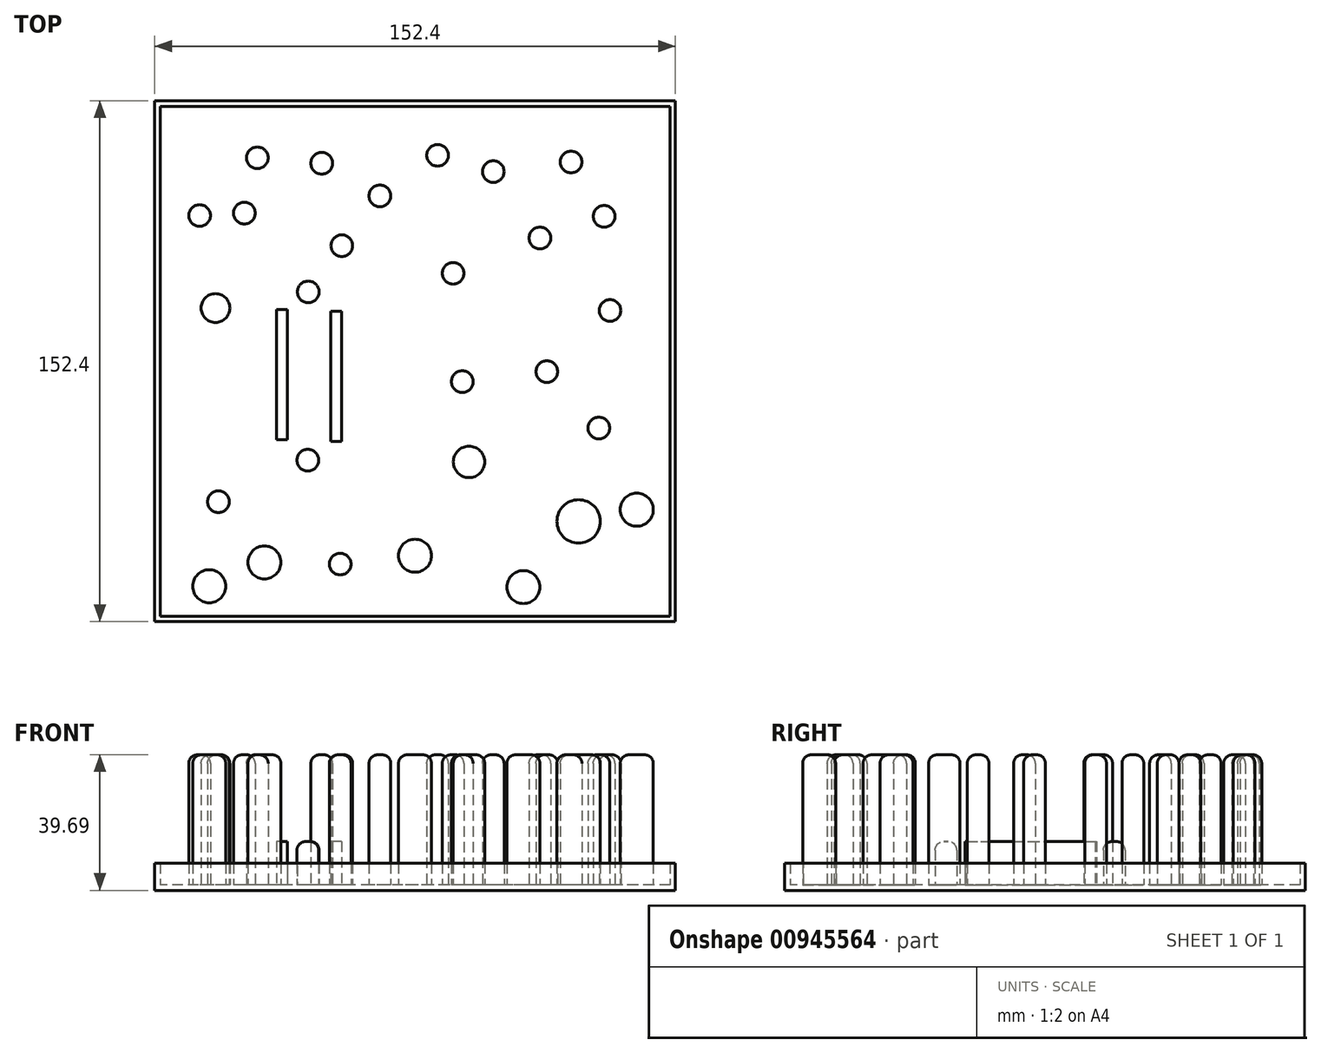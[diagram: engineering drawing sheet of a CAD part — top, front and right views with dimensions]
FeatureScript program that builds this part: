
annotation { "Feature Type Name" : "Feature", "Feature Type Description" : "" }
export const myFeature = defineFeature(function(context is Context, id is Id, definition is map)
    precondition{}
    {
        {
            var Q0;
            Q0=qCreatedBy(makeId("Top.planeOp"),FACE);
            var sketch = newSketch(context, id + "F0", { "sketchPlane" : qUnion([Q0])});
            skLineSegment(sketch, "E0.bottom", {"start": v(76.2, 76.2) * mm, "end": v(-76.2, 76.2) * mm});
            skLineSegment(sketch, "E0.top", {"start": v(76.2, -76.2) * mm, "end": v(-76.2, -76.2) * mm});
            skLineSegment(sketch, "E0.left", {"start": v(76.2, 76.2) * mm, "end": v(76.2, -76.2) * mm});
            skLineSegment(sketch, "E0.right", {"start": v(-76.2, 76.2) * mm, "end": v(-76.2, -76.2) * mm});
            skPoint(sketch, "E0.middle", {"position": v(0, 0) * mm});
            skSolve(sketch);
        }
        {
            var Q0;
            Q0=makeQuery(id+"F0.imprint","IMPRINT",FACE,{"disambiguationData":[TD([[makeQuery(id+"F0.imprint","IMPRINT",EDGE,{"derivedFrom":sQuery(id+"F0.wireOp",EDGE,"E0.bottom")}),1.0]])]});
            extrude(context, id + "F1", {"entities" : qUnion([Q0]), "depth" : 1.59 * mm, "offsetDistance" : 25.4 * mm});
        }
        {
            var Q0;
            Q0=makeQuery(id+"F1.opExtrude","CAP_FACE",FACE,{"disambiguationData":[OSD([sQuery(id+"F0.wireOp",EDGE,"E0.bottom"),sQuery(id+"F0.wireOp",EDGE,"E0.top"),sQuery(id+"F0.wireOp",EDGE,"E0.left"),sQuery(id+"F0.wireOp",EDGE,"E0.right")])],"isStart":false});
            var sketch = newSketch(context, id + "F2", { "sketchPlane" : qUnion([Q0])});
            skCircle(sketch, "E1", {"center": v(55.35, 42.37) * mm, "radius": 3.18 * mm});
            skLineSegment(sketch, "E2.bottom", {"start": v(74.61, 74.61) * mm, "end": v(-74.61, 74.61) * mm});
            skLineSegment(sketch, "E2.top", {"start": v(74.61, -74.61) * mm, "end": v(-74.61, -74.61) * mm});
            skLineSegment(sketch, "E2.left", {"start": v(74.61, 74.61) * mm, "end": v(74.61, -74.61) * mm});
            skLineSegment(sketch, "E2.right", {"start": v(-74.61, 74.61) * mm, "end": v(-74.61, -74.61) * mm});
            skPoint(sketch, "E2.middle", {"position": v(0, 0) * mm});
            skCircle(sketch, "E3", {"center": v(15.8, -29.49) * mm, "radius": 4.6 * mm});
            skCircle(sketch, "E4", {"center": v(53.8, -19.58) * mm, "radius": 3.18 * mm});
            skCircle(sketch, "E5", {"center": v(-31.25, 20.26) * mm, "radius": 3.18 * mm});
            skCircle(sketch, "E6", {"center": v(36.56, 36.04) * mm, "radius": 3.18 * mm});
            skCircle(sketch, "E7", {"center": v(-31.4, -28.99) * mm, "radius": 3.18 * mm});
            skLineSegment(sketch, "E8.bottom", {"start": v(-21.54, -23.45) * mm, "end": v(-24.72, -23.45) * mm});
            skLineSegment(sketch, "E8.top", {"start": v(-21.54, 14.65) * mm, "end": v(-24.72, 14.65) * mm});
            skLineSegment(sketch, "E8.left", {"start": v(-21.54, -23.45) * mm, "end": v(-21.54, 14.65) * mm});
            skLineSegment(sketch, "E8.right", {"start": v(-24.72, -23.45) * mm, "end": v(-24.72, 14.65) * mm});
            skLineSegment(sketch, "E9.bottom", {"start": v(-37.42, -22.96) * mm, "end": v(-40.6, -22.96) * mm});
            skLineSegment(sketch, "E9.top", {"start": v(-37.42, 15.14) * mm, "end": v(-40.6, 15.14) * mm});
            skLineSegment(sketch, "E9.left", {"start": v(-37.42, -22.96) * mm, "end": v(-37.42, 15.14) * mm});
            skLineSegment(sketch, "E9.right", {"start": v(-40.6, -22.96) * mm, "end": v(-40.6, 15.14) * mm});
            skCircle(sketch, "E10", {"center": v(11.14, 25.72) * mm, "radius": 3.18 * mm});
            skCircle(sketch, "E11", {"center": v(31.72, -66.13) * mm, "radius": 4.83 * mm});
            skCircle(sketch, "E12", {"center": v(-10.29, 48.37) * mm, "radius": 3.18 * mm});
            skCircle(sketch, "E13", {"center": v(22.9, 55.47) * mm, "radius": 3.18 * mm});
            skCircle(sketch, "E14", {"center": v(38.57, -3.06) * mm, "radius": 3.17 * mm});
            skCircle(sketch, "E15", {"center": v(-49.96, 43.35) * mm, "radius": 3.18 * mm});
            skCircle(sketch, "E16", {"center": v(-60.25, -65.88) * mm, "radius": 4.83 * mm});
            skCircle(sketch, "E17", {"center": v(-21.92, -59.4) * mm, "radius": 3.18 * mm});
            skCircle(sketch, "E18", {"center": v(-21.43, 33.8) * mm, "radius": 3.18 * mm});
            skCircle(sketch, "E19", {"center": v(0, -56.94) * mm, "radius": 4.83 * mm});
            skCircle(sketch, "E20", {"center": v(6.61, 60.25) * mm, "radius": 3.18 * mm});
            skCircle(sketch, "E21", {"center": v(-46.17, 59.51) * mm, "radius": 3.18 * mm});
            skCircle(sketch, "E22", {"center": v(-58.41, 15.55) * mm, "radius": 4.21 * mm});
            skCircle(sketch, "E23", {"center": v(-57.56, -41.15) * mm, "radius": 3.18 * mm});
            skCircle(sketch, "E24", {"center": v(-44.08, -58.9) * mm, "radius": 4.83 * mm});
            skCircle(sketch, "E25", {"center": v(-63.07, 42.62) * mm, "radius": 3.18 * mm});
            skCircle(sketch, "E26", {"center": v(-27.3, 57.92) * mm, "radius": 3.18 * mm});
            skCircle(sketch, "E27", {"center": v(47.88, -46.9) * mm, "radius": 6.35 * mm});
            skCircle(sketch, "E28", {"center": v(13.84, -6) * mm, "radius": 3.18 * mm});
            skCircle(sketch, "E29", {"center": v(57.07, 14.82) * mm, "radius": 3.18 * mm});
            skCircle(sketch, "E30", {"center": v(45.68, 58.29) * mm, "radius": 3.18 * mm});
            skCircle(sketch, "E31", {"center": v(64.9, -43.47) * mm, "radius": 4.83 * mm});
            skSolve(sketch);
        }
        {
            var Q0;
            Q0=makeQuery(id+"F2.imprint","IMPRINT",FACE,{"disambiguationData":[TD([[makeQuery(id+"F2.imprint","IMPRINT",EDGE,{"derivedFrom":sQuery(id+"F2.wireOp",EDGE,"E2.bottom")}),-1.0]])]});
            extrude(context, id + "F3", {"entities" : qUnion([Q0]), "operationType" : NewBodyOperationType.ADD, "depth" : 6.35 * mm, "offsetDistance" : 25.4 * mm});
        }
        {
            var Q0;
            Q0=makeQuery(id+"F2.imprint","IMPRINT",FACE,{"disambiguationData":[TD([[makeQuery(id+"F2.imprint","IMPRINT",EDGE,{"derivedFrom":sQuery(id+"F2.wireOp",EDGE,"E7")}),1.0]])]});
            var Q1;
            Q1=makeQuery(id+"F2.imprint","IMPRINT",FACE,{"disambiguationData":[TD([[makeQuery(id+"F2.imprint","IMPRINT",EDGE,{"derivedFrom":sQuery(id+"F2.wireOp",EDGE,"E5")}),1.0]])]});
            var Q2;
            Q2=makeQuery(id+"F2.imprint","IMPRINT",FACE,{"disambiguationData":[TD([[makeQuery(id+"F2.imprint","IMPRINT",EDGE,{"derivedFrom":sQuery(id+"F2.wireOp",EDGE,"E8.bottom")}),-1.0]])]});
            var Q3;
            Q3=makeQuery(id+"F2.imprint","IMPRINT",FACE,{"disambiguationData":[TD([[makeQuery(id+"F2.imprint","IMPRINT",EDGE,{"derivedFrom":sQuery(id+"F2.wireOp",EDGE,"E9.bottom")}),-1.0]])]});
            extrude(context, id + "F4", {"entities" : qUnion([Q0, Q1, Q2, Q3]), "operationType" : NewBodyOperationType.ADD, "depth" : 12.7 * mm, "offsetDistance" : 25.4 * mm});
        }
        {
            var Q0;
            Q0=makeQuery(id+"F2.imprint","IMPRINT",FACE,{"disambiguationData":[TD([[makeQuery(id+"F2.imprint","IMPRINT",EDGE,{"derivedFrom":sQuery(id+"F2.wireOp",EDGE,"E3")}),1.0]])]});
            var Q1;
            Q1=makeQuery(id+"F2.imprint","IMPRINT",FACE,{"disambiguationData":[TD([[makeQuery(id+"F2.imprint","IMPRINT",EDGE,{"derivedFrom":sQuery(id+"F2.wireOp",EDGE,"E4")}),1.0]])]});
            var Q2;
            Q2=makeQuery(id+"F2.imprint","IMPRINT",FACE,{"disambiguationData":[TD([[makeQuery(id+"F2.imprint","IMPRINT",EDGE,{"derivedFrom":sQuery(id+"F2.wireOp",EDGE,"E6")}),1.0]])]});
            var Q3;
            Q3=makeQuery(id+"F2.imprint","IMPRINT",FACE,{"disambiguationData":[TD([[makeQuery(id+"F2.imprint","IMPRINT",EDGE,{"derivedFrom":sQuery(id+"F2.wireOp",EDGE,"E1")}),1.0]])]});
            var Q4;
            Q4=makeQuery(id+"F2.imprint","IMPRINT",FACE,{"disambiguationData":[TD([[makeQuery(id+"F2.imprint","IMPRINT",EDGE,{"derivedFrom":sQuery(id+"F2.wireOp",EDGE,"E30")}),1.0]])]});
            var Q5;
            Q5=makeQuery(id+"F2.imprint","IMPRINT",FACE,{"disambiguationData":[TD([[makeQuery(id+"F2.imprint","IMPRINT",EDGE,{"derivedFrom":sQuery(id+"F2.wireOp",EDGE,"E13")}),1.0]])]});
            var Q6;
            Q6=makeQuery(id+"F2.imprint","IMPRINT",FACE,{"disambiguationData":[TD([[makeQuery(id+"F2.imprint","IMPRINT",EDGE,{"derivedFrom":sQuery(id+"F2.wireOp",EDGE,"E20")}),1.0]])]});
            var Q7;
            Q7=makeQuery(id+"F2.imprint","IMPRINT",FACE,{"disambiguationData":[TD([[makeQuery(id+"F2.imprint","IMPRINT",EDGE,{"derivedFrom":sQuery(id+"F2.wireOp",EDGE,"E12")}),1.0]])]});
            var Q8;
            Q8=makeQuery(id+"F2.imprint","IMPRINT",FACE,{"disambiguationData":[TD([[makeQuery(id+"F2.imprint","IMPRINT",EDGE,{"derivedFrom":sQuery(id+"F2.wireOp",EDGE,"E26")}),1.0]])]});
            var Q9;
            Q9=makeQuery(id+"F2.imprint","IMPRINT",FACE,{"disambiguationData":[TD([[makeQuery(id+"F2.imprint","IMPRINT",EDGE,{"derivedFrom":sQuery(id+"F2.wireOp",EDGE,"E21")}),1.0]])]});
            var Q10;
            Q10=makeQuery(id+"F2.imprint","IMPRINT",FACE,{"disambiguationData":[TD([[makeQuery(id+"F2.imprint","IMPRINT",EDGE,{"derivedFrom":sQuery(id+"F2.wireOp",EDGE,"E15")}),1.0]])]});
            var Q11;
            Q11=makeQuery(id+"F2.imprint","IMPRINT",FACE,{"disambiguationData":[TD([[makeQuery(id+"F2.imprint","IMPRINT",EDGE,{"derivedFrom":sQuery(id+"F2.wireOp",EDGE,"E25")}),1.0]])]});
            var Q12;
            Q12=makeQuery(id+"F2.imprint","IMPRINT",FACE,{"disambiguationData":[TD([[makeQuery(id+"F2.imprint","IMPRINT",EDGE,{"derivedFrom":sQuery(id+"F2.wireOp",EDGE,"E22")}),1.0]])]});
            var Q13;
            Q13=makeQuery(id+"F2.imprint","IMPRINT",FACE,{"disambiguationData":[TD([[makeQuery(id+"F2.imprint","IMPRINT",EDGE,{"derivedFrom":sQuery(id+"F2.wireOp",EDGE,"E23")}),1.0]])]});
            var Q14;
            Q14=makeQuery(id+"F2.imprint","IMPRINT",FACE,{"disambiguationData":[TD([[makeQuery(id+"F2.imprint","IMPRINT",EDGE,{"derivedFrom":sQuery(id+"F2.wireOp",EDGE,"E24")}),1.0]])]});
            var Q15;
            Q15=makeQuery(id+"F2.imprint","IMPRINT",FACE,{"disambiguationData":[TD([[makeQuery(id+"F2.imprint","IMPRINT",EDGE,{"derivedFrom":sQuery(id+"F2.wireOp",EDGE,"E19")}),1.0]])]});
            var Q16;
            Q16=makeQuery(id+"F2.imprint","IMPRINT",FACE,{"disambiguationData":[TD([[makeQuery(id+"F2.imprint","IMPRINT",EDGE,{"derivedFrom":sQuery(id+"F2.wireOp",EDGE,"E11")}),1.0]])]});
            var Q17;
            Q17=makeQuery(id+"F2.imprint","IMPRINT",FACE,{"disambiguationData":[TD([[makeQuery(id+"F2.imprint","IMPRINT",EDGE,{"derivedFrom":sQuery(id+"F2.wireOp",EDGE,"E27")}),1.0]])]});
            var Q18;
            Q18=makeQuery(id+"F2.imprint","IMPRINT",FACE,{"disambiguationData":[TD([[makeQuery(id+"F2.imprint","IMPRINT",EDGE,{"derivedFrom":sQuery(id+"F2.wireOp",EDGE,"E31")}),1.0]])]});
            var Q19;
            Q19=makeQuery(id+"F2.imprint","IMPRINT",FACE,{"disambiguationData":[TD([[makeQuery(id+"F2.imprint","IMPRINT",EDGE,{"derivedFrom":sQuery(id+"F2.wireOp",EDGE,"E10")}),1.0]])]});
            var Q20;
            Q20=makeQuery(id+"F2.imprint","IMPRINT",FACE,{"disambiguationData":[TD([[makeQuery(id+"F2.imprint","IMPRINT",EDGE,{"derivedFrom":sQuery(id+"F2.wireOp",EDGE,"E18")}),1.0]])]});
            var Q21;
            Q21=makeQuery(id+"F2.imprint","IMPRINT",FACE,{"disambiguationData":[TD([[makeQuery(id+"F2.imprint","IMPRINT",EDGE,{"derivedFrom":sQuery(id+"F2.wireOp",EDGE,"E14")}),1.0]])]});
            var Q22;
            Q22=makeQuery(id+"F2.imprint","IMPRINT",FACE,{"disambiguationData":[TD([[makeQuery(id+"F2.imprint","IMPRINT",EDGE,{"derivedFrom":sQuery(id+"F2.wireOp",EDGE,"E28")}),1.0]])]});
            var Q23;
            Q23=makeQuery(id+"F2.imprint","IMPRINT",FACE,{"disambiguationData":[TD([[makeQuery(id+"F2.imprint","IMPRINT",EDGE,{"derivedFrom":sQuery(id+"F2.wireOp",EDGE,"E29")}),1.0]])]});
            var Q24;
            Q24=makeQuery(id+"F2.imprint","IMPRINT",FACE,{"disambiguationData":[TD([[makeQuery(id+"F2.imprint","IMPRINT",EDGE,{"derivedFrom":sQuery(id+"F2.wireOp",EDGE,"E16")}),1.0]])]});
            var Q25;
            Q25=makeQuery(id+"F2.imprint","IMPRINT",FACE,{"disambiguationData":[TD([[makeQuery(id+"F2.imprint","IMPRINT",EDGE,{"derivedFrom":sQuery(id+"F2.wireOp",EDGE,"E17")}),1.0]])]});
            extrude(context, id + "F5", {"entities" : qUnion([Q0, Q1, Q2, Q3, Q4, Q5, Q6, Q7, Q8, Q9, Q10, Q11, Q12, Q13, Q14, Q15, Q16, Q17, Q18, Q19, Q20, Q21, Q22, Q23, Q24, Q25]), "operationType" : NewBodyOperationType.ADD, "depth" : 38.1 * mm, "offsetDistance" : 25.4 * mm});
        }
        {
            var Q0;
            Q0=makeQuery(id+"F5.opExtrude","CAP_EDGE",EDGE,{"disambiguationData":[OSD([sQuery(id+"F2.wireOp",EDGE,"E30")])],"isStart":false});
            var Q1;
            Q1=makeQuery(id+"F5.opExtrude","CAP_EDGE",EDGE,{"disambiguationData":[OSD([sQuery(id+"F2.wireOp",EDGE,"E6")])],"isStart":false});
            var Q2;
            Q2=makeQuery(id+"F5.opExtrude","CAP_EDGE",EDGE,{"disambiguationData":[OSD([sQuery(id+"F2.wireOp",EDGE,"E13")])],"isStart":false});
            var Q3;
            Q3=makeQuery(id+"F5.opExtrude","CAP_EDGE",EDGE,{"disambiguationData":[OSD([sQuery(id+"F2.wireOp",EDGE,"E20")])],"isStart":false});
            var Q4;
            Q4=makeQuery(id+"F5.opExtrude","CAP_EDGE",EDGE,{"disambiguationData":[OSD([sQuery(id+"F2.wireOp",EDGE,"E1")])],"isStart":false});
            var Q5;
            Q5=makeQuery(id+"F5.opExtrude","CAP_EDGE",EDGE,{"disambiguationData":[OSD([sQuery(id+"F2.wireOp",EDGE,"E29")])],"isStart":false});
            var Q6;
            Q6=makeQuery(id+"F5.opExtrude","CAP_EDGE",EDGE,{"disambiguationData":[OSD([sQuery(id+"F2.wireOp",EDGE,"E10")])],"isStart":false});
            var Q7;
            Q7=makeQuery(id+"F5.opExtrude","CAP_EDGE",EDGE,{"disambiguationData":[OSD([sQuery(id+"F2.wireOp",EDGE,"E12")])],"isStart":false});
            var Q8;
            Q8=makeQuery(id+"F5.opExtrude","CAP_EDGE",EDGE,{"disambiguationData":[OSD([sQuery(id+"F2.wireOp",EDGE,"E26")])],"isStart":false});
            var Q9;
            Q9=makeQuery(id+"F5.opExtrude","CAP_EDGE",EDGE,{"disambiguationData":[OSD([sQuery(id+"F2.wireOp",EDGE,"E21")])],"isStart":false});
            var Q10;
            Q10=makeQuery(id+"F5.opExtrude","CAP_EDGE",EDGE,{"disambiguationData":[OSD([sQuery(id+"F2.wireOp",EDGE,"E15")])],"isStart":false});
            var Q11;
            Q11=makeQuery(id+"F5.opExtrude","CAP_EDGE",EDGE,{"disambiguationData":[OSD([sQuery(id+"F2.wireOp",EDGE,"E4")])],"isStart":false});
            var Q12;
            Q12=makeQuery(id+"F5.opExtrude","CAP_FACE",FACE,{"disambiguationData":[OSD([sQuery(id+"F2.wireOp",EDGE,"E31")])],"isStart":false});
            var Q13;
            Q13=makeQuery(id+"F5.opExtrude","CAP_FACE",FACE,{"disambiguationData":[OSD([sQuery(id+"F2.wireOp",EDGE,"E27")])],"isStart":false});
            var Q14;
            Q14=makeQuery(id+"F5.opExtrude","CAP_FACE",FACE,{"disambiguationData":[OSD([sQuery(id+"F2.wireOp",EDGE,"E3")])],"isStart":false});
            var Q15;
            Q15=makeQuery(id+"F5.opExtrude","CAP_EDGE",EDGE,{"disambiguationData":[OSD([sQuery(id+"F2.wireOp",EDGE,"E28")])],"isStart":false});
            var Q16;
            Q16=makeQuery(id+"F5.opExtrude","CAP_EDGE",EDGE,{"disambiguationData":[OSD([sQuery(id+"F2.wireOp",EDGE,"E14")])],"isStart":false});
            var Q17;
            Q17=makeQuery(id+"F5.opExtrude","CAP_EDGE",EDGE,{"disambiguationData":[OSD([sQuery(id+"F2.wireOp",EDGE,"E18")])],"isStart":false});
            var Q18;
            Q18=makeQuery(id+"F5.opExtrude","CAP_FACE",FACE,{"disambiguationData":[OSD([sQuery(id+"F2.wireOp",EDGE,"E22")])],"isStart":false});
            var Q19;
            Q19=makeQuery(id+"F5.opExtrude","CAP_EDGE",EDGE,{"disambiguationData":[OSD([sQuery(id+"F2.wireOp",EDGE,"E25")])],"isStart":false});
            var Q20;
            Q20=makeQuery(id+"F4.opExtrude","CAP_EDGE",EDGE,{"disambiguationData":[OSD([sQuery(id+"F2.wireOp",EDGE,"E5")])],"isStart":false});
            var Q21;
            Q21=makeQuery(id+"F4.opExtrude","CAP_EDGE",EDGE,{"disambiguationData":[OSD([sQuery(id+"F2.wireOp",EDGE,"E7")])],"isStart":false});
            var Q22;
            Q22=makeQuery(id+"F5.opExtrude","CAP_FACE",FACE,{"disambiguationData":[OSD([sQuery(id+"F2.wireOp",EDGE,"E19")])],"isStart":false});
            var Q23;
            Q23=makeQuery(id+"F5.opExtrude","CAP_FACE",FACE,{"disambiguationData":[OSD([sQuery(id+"F2.wireOp",EDGE,"E11")])],"isStart":false});
            var Q24;
            Q24=makeQuery(id+"F5.opExtrude","CAP_EDGE",EDGE,{"disambiguationData":[OSD([sQuery(id+"F2.wireOp",EDGE,"E17")])],"isStart":false});
            var Q25;
            Q25=makeQuery(id+"F5.opExtrude","CAP_FACE",FACE,{"disambiguationData":[OSD([sQuery(id+"F2.wireOp",EDGE,"E24")])],"isStart":false});
            var Q26;
            Q26=makeQuery(id+"F5.opExtrude","CAP_EDGE",EDGE,{"disambiguationData":[OSD([sQuery(id+"F2.wireOp",EDGE,"E23")])],"isStart":false});
            var Q27;
            Q27=makeQuery(id+"F5.opExtrude","CAP_FACE",FACE,{"disambiguationData":[OSD([sQuery(id+"F2.wireOp",EDGE,"E16")])],"isStart":false});
            fillet(context, id + "F6", {"entities" : qUnion([Q0, Q1, Q2, Q3, Q4, Q5, Q6, Q7, Q8, Q9, Q10, Q11, Q12, Q13, Q14, Q15, Q16, Q17, Q18, Q19, Q20, Q21, Q22, Q23, Q24, Q25, Q26, Q27]), "radius" : 2.54 * mm, "tangentPropagation" : true, "allowEdgeOverflow" : false});
        }
    });
